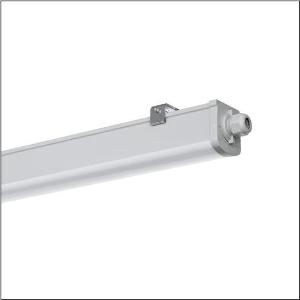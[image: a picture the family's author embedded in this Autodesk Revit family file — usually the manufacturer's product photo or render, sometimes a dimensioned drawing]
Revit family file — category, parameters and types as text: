
# Revit family: monsun_r__31_51fa207p460b_ddf4
name_source: partatom
category: Lighting Fixtures
units: mm (PartAtom-declared; Revit-internal decimal feet)

## family parameters
Cut with Voids When Loaded = No
Host = Face
Light Source = No
Part Type = Normal
Room Calculation Point = No
Round Connector Dimension = Use Diameter
Shared = No

## types (1)
- Monsun® 31 (1 x LED, 6700 lm, 50 W, 4000K)
    Apparent Load = 50 VA
    CIE Flux Codes = 42 72 91 92 100
    Color Rendering = 80
    Color Temperature = 4000K
    Default Elevation = 1800 mm
    Description = Monsun® 31, damp-proof luminaire, primary optical cover: diffuser, of PC, frosted, light emission: direct distribution, primary light characteristic: symmetric, installation type: surface-mounted, LED, rated luminous flux: 6.700lm, luminous efficacy: 134lm/W, light colour: 840, colour temperature: 4000K, control gear: ECG, with terminal, 3+1-pole, max. 2.5mm², through-wiring: 3x 2.5mm² + 1x 1.5mm², mains connection: 220..240V, AC, 50/60Hz, rated input power: 50W, housing, luminaire housing, of PC, light grey (RAL 7035), length: 1.458mm, width: 68mm, height: 76mm, protection rating (complete): IP66, insulation class (complete): insulation class II (safety insulation), certification: CE, ENEC, UKCA, protection symbol: D, impact resistance: IK08, permissible operating ambient temperature: -20..+40°C, corresponds to IFS (International Featured Standards) requirements for safety and quality in the food industry, contact your sales advisor before using the luminaires in applications with unclear chemical exposure, large temperature fluctuations or condensation-forming humidity, packaging unit: 1 piece
    Height = 77 mm
    Lamp = 1 x LED
    Lamp Light Flux = 6700 lm
    Lamp Power = 50 W
    Lamp count = 1
    Length = 1518 mm
    Luminous efficacy = 134 lm/W
    Manufacturer = Siteco
    ModVariant = No
    Model = 51FA207P460B
    Mounting Place = Ceiling
    Mounting Type = Surface mounted
    Number of Poles = 1
    OnlyDefault = Yes
    Power Factor = 1
    Product Name = Monsun® 31
    Product group = damp-proof luminaire
    ProductGroupID = 300
    Protection Class = Protection class II
    Protection Degree = IP 66
    RLX_Detail_Level = 1
    RLX_Emergency_Light_Flux = 0 lm
    RLX_Emergency_Type = 0
    RLX_Emergency_Type_DB = No
    RlxData = <blob elided: 33165 chars, md5=1c2e37ef>
    Socket = socket
    Standby Power = 0 W
    System Light Flux = 6700 lm
    System Power = 50 W
    Type Comments = Product without accessories
    Type Image = l_1006174.jpg
    URL = http://relux.com
    VarID = ---
    Voltage = 0 V
    Weight = 0.00 kg
    Width = 69 mm

## geometry (parser evidence)
native form markers: Blend x4, Sweep x11
no freeform markers — native parametric forms only
